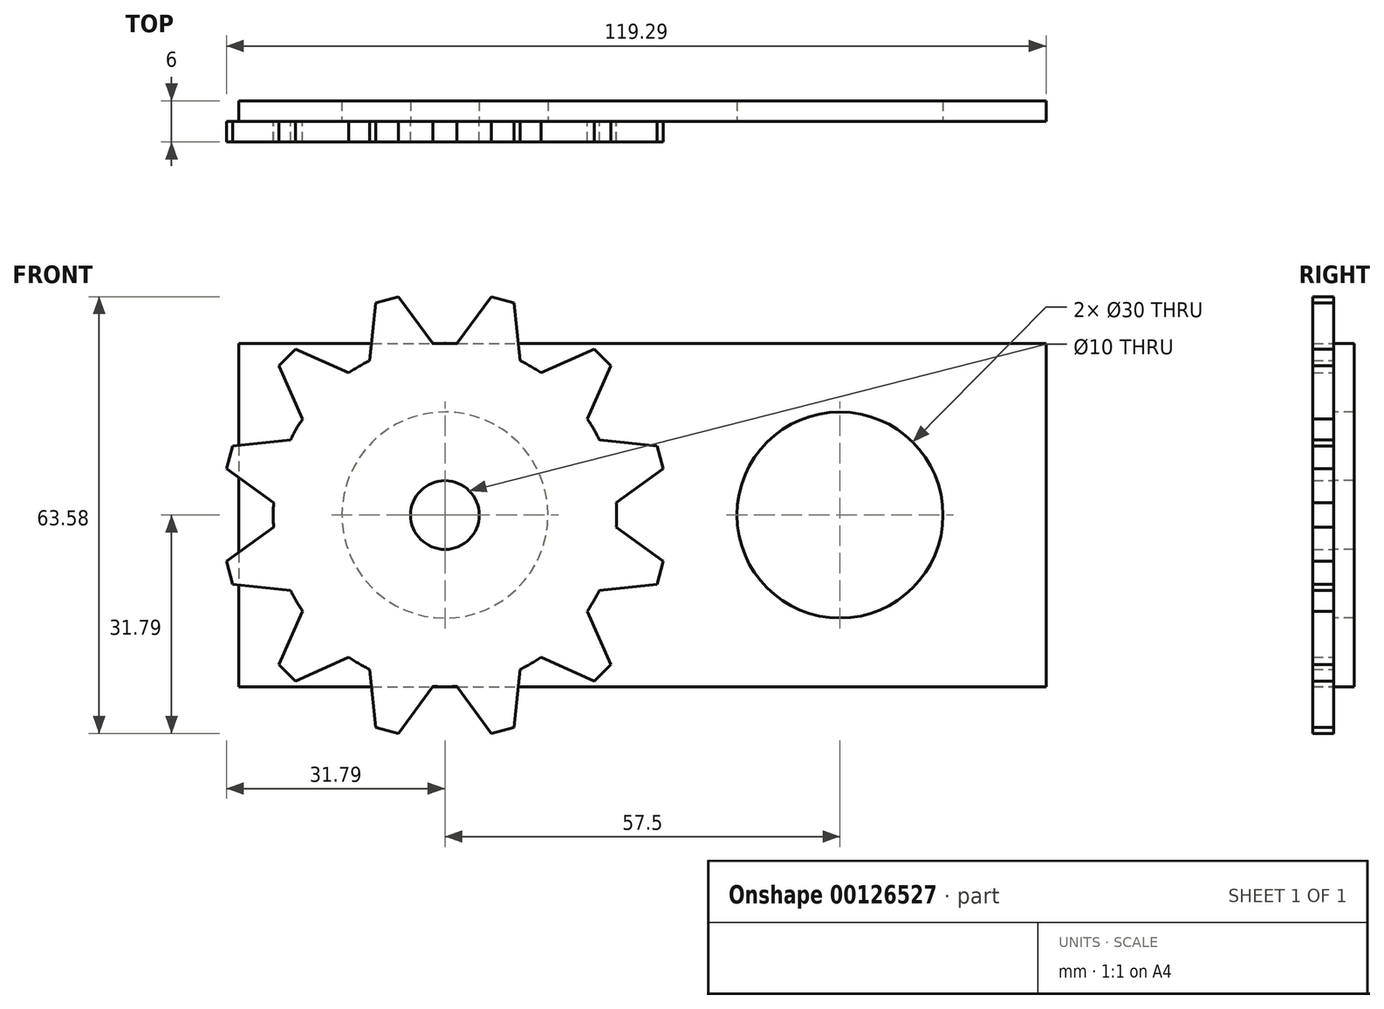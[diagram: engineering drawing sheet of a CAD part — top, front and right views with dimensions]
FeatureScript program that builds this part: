
annotation { "Feature Type Name" : "Feature", "Feature Type Description" : "" }
export const myFeature = defineFeature(function(context is Context, id is Id, definition is map)
    precondition{}
    {
        {
            var Q0;
            Q0=qCreatedBy(makeId("Front.planeOp"),FACE);
            var sketch = newSketch(context, id + "F7", { "sketchPlane" : qUnion([Q0])});
            skCircle(sketch, "E0", {"center": v(0, 0) * mm, "radius": 25 * mm, "construction": true});
            skLineSegment(sketch, "E1", {"start": v(0, 25) * mm, "end": v(12.5, 21.65) * mm, "construction": true});
            skLineSegment(sketch, "E2", {"start": v(6.25, 23.33) * mm, "end": v(8.83, 32.96) * mm, "construction": true});
            skLineSegment(sketch, "E3", {"start": v(0, 0) * mm, "end": v(0, 25) * mm, "construction": true});
            skLineSegment(sketch, "E4", {"start": v(0, 0) * mm, "end": v(12.5, 21.65) * mm, "construction": true});
            skCircle(sketch, "E5", {"center": v(0, 0) * mm, "radius": 32.5 * mm, "construction": true});
            skLineSegment(sketch, "E6", {"start": v(6.74, 31.8) * mm, "end": v(1.76, 24.94) * mm});
            skLineSegment(sketch, "E7.MirrorCS", {"start": v(10.06, 30.9) * mm, "end": v(10.94, 22.48) * mm});
            skLineSegment(sketch, "E8", {"start": v(6.74, 31.8) * mm, "end": v(10.06, 30.9) * mm});
            skLineSegment(sketch, "E9", {"start": v(1.76, 24.94) * mm, "end": v(10.94, 22.48) * mm});
            skSolve(sketch);
        }
        {
            var Q0;
            Q0=qSketchRegion(id+"F7",true);
            extrude(context, id + "F0", {"entities" : qUnion([Q0]), "depth" : 3 * mm});
        }
        {
            var Q0;
            Q0=qCreatedBy(makeId("Top.planeOp"),FACE);
            var sketch = newSketch(context, id + "F8", { "sketchPlane" : qUnion([Q0])});
            skLineSegment(sketch, "E10", {"start": v(0, 0) * mm, "end": v(0, -32.55) * mm, "construction": true});
            skSolve(sketch);
        }
        {
            var Q0;
            Q0=qCreatedBy(makeId("Front.planeOp"),FACE);
            var sketch = newSketch(context, id + "F1", { "sketchPlane" : qUnion([Q0])});
            skCircle(sketch, "E11", {"center": v(0, 0) * mm, "radius": 25 * mm});
            skCircle(sketch, "E12", {"center": v(0, 0) * mm, "radius": 5 * mm});
            skSolve(sketch);
        }
        {
            var Q0;
            Q0=qSketchRegion(id+"F1",true);
            extrude(context, id + "F2", {"entities" : qUnion([Q0]), "depth" : 3 * mm});
        }
        {
            var Q0;
            Q0=makeQuery(id+"F0.opExtrude","SWEPT_BODY",BODY,{"disambiguationData":[OSD([sQuery(id+"F7.wireOp",EDGE,"E6"),sQuery(id+"F7.wireOp",EDGE,"E7.MirrorCS"),sQuery(id+"F7.wireOp",EDGE,"E8"),sQuery(id+"F7.wireOp",EDGE,"E9")])]});
            var Q1;
            Q1=sQuery(id+"F8.wireOp",EDGE,"E10");
            circularPattern(context, id + "F9", {"operationType" : NewBodyOperationType.ADD, "entities" : qUnion([Q0]), "axis" : qUnion([Q1]), "angle" : 30 * degree, "instanceCount" : 12});
        }
        {
            var Q0;
            Q0=qCreatedBy(makeId("Front.planeOp"),FACE);
            var sketch = newSketch(context, id + "F3", { "sketchPlane" : qUnion([Q0])});
            skLineSegment(sketch, "E13.bottom", {"start": v(-30, 25) * mm, "end": v(87.5, 25) * mm});
            skLineSegment(sketch, "E13.top", {"start": v(-30, -25) * mm, "end": v(87.5, -25) * mm});
            skLineSegment(sketch, "E13.left", {"start": v(-30, 25) * mm, "end": v(-30, -25) * mm});
            skLineSegment(sketch, "E13.right", {"start": v(87.5, 25) * mm, "end": v(87.5, -25) * mm});
            skLineSegment(sketch, "E14", {"start": v(-30, 0) * mm, "end": v(87.5, 0) * mm, "construction": true});
            skCircle(sketch, "E15", {"center": v(0, 0) * mm, "radius": 15 * mm});
            skCircle(sketch, "E16", {"center": v(57.5, 0) * mm, "radius": 15 * mm});
            skLineSegment(sketch, "E17", {"start": v(0, 25) * mm, "end": v(0, 0) * mm, "construction": true});
            skSolve(sketch);
        }
        {
            var Q0;
            Q0=qSketchRegion(id+"F3",true);
            extrude(context, id + "F4", {"entities" : qUnion([Q0]), "oppositeDirection" : true, "depth" : 3 * mm});
        }
        {
            var Q0;
            Q0=qCreatedBy(makeId("Front.planeOp"),FACE);
            var sketch = newSketch(context, id + "F5", { "sketchPlane" : qUnion([Q0])});
            skCircle(sketch, "E18", {"center": v(0, 0) * mm, "radius": 5 * mm});
            skSolve(sketch);
        }
        {
            var Q0;
            Q0=qSketchRegion(id+"F5",true);
            extrude(context, id + "F6", {"entities" : qUnion([Q0]), "operationType" : NewBodyOperationType.ADD, "oppositeDirection" : true, "depth" : 3 * mm});
        }
    });
